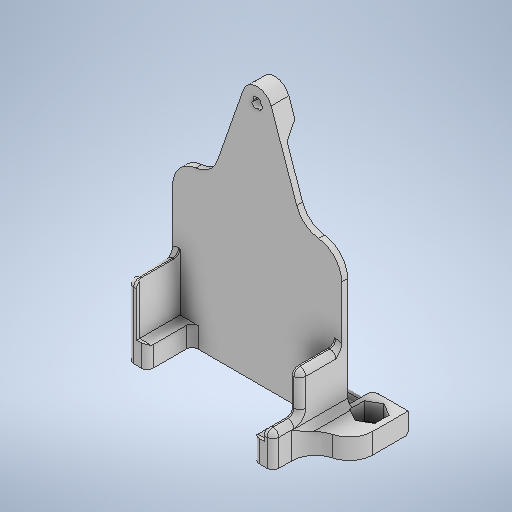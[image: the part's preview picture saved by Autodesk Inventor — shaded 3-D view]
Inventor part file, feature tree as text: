
AUTODESK INVENTOR PART (.ipt)
format: ipt  version: 2025.3 (Build 293356000, 356)  size: 1,111,552 bytes
history: native  units: in
note: dims shown in document units (in); Inventor stores cm internally (conversion verified against a paired STEP export)
features: sketch x16, extrude x14, fillet x5, chamfer x3, hole x1
ambient origin geometry x8: Origin, YZ Plane, XZ Plane, XY Plane, X Axis, Y Axis, Z Axis, Center Point
bodies: Solid1 (feature_tree)
feature tree (39):
  extrude  "Extrusion1"  Depth=0.3937in
  extrude  "Extrusion2"  Depth=0.0787in
  extrude  "Extrusion3"  Depth=0.6098in
  extrude  "Extrusion4"  Depth=0.1575in TaperAngle=0.0deg
  extrude  "Extrusion5"  Depth=0.878in TaperAngle=0.0deg
  extrude  "Extrusion6"  Depth=0.0394in TaperAngle=0.0deg
  extrude  "Extrusion8"  Depth=0.2598in
  hole  "Hole1"  [1 undecoded]
  extrude  "Extrusion15"  Depth=1.128in
  chamfer  "Chamfer1"  Distance=0.52in
  chamfer  "Chamfer2"  Distance=1.1811in Angle=360.0deg
  chamfer  "Chamfer3"  Distance=0.3937in
  extrude  "Extrusion17"  Depth=0.0787in
  extrude  "Extrusion18"  Depth=0.0787in
  fillet  "Fillet6"  Radius=0.7874in
  fillet  "Fillet7"  Radius=0.7874in
  fillet  "Fillet8"  Radius=0.0984in
  extrude  "Extrusion20"  Depth=0.0787in
  extrude  "Extrusion21"  Depth=0.0787in
  extrude  "Extrusion22"  Depth=0.0787in
  fillet  "Fillet9"  Radius=0.1181in
  fillet  "Fillet10"  Radius=0.2622in
  extrude  "Extrusion23"  Depth=0.0787in
  sketch  "Sketch1"  dims[d2=0.3937in d3=1.1516in]
  sketch  "Sketch2"  dims[d26=1.2197in d27=0.6098in]
  sketch  "Sketch3"  dims[d28=0.0in d40=0.1575in d41=0.0in]
  sketch  "Sketch4"  dims[d73=0.5593in d74=0.0in d79=0.878in d80=0.0in]
  sketch  "Sketch5"  dims[d89=0.0394in d90=0.0in d95=0.0394in d96=0.0in]
  sketch  "Sketch6"  dims[d100=0.2598in d101=0.2598in]
  sketch  "Sketch9"  dims[d102=0.0984in d103=0.0984in]
  sketch  "Sketch11"  dims[d112=2.2559in d113=1.128in]
  sketch  "Sketch18"  dims[d114=3.2323in d120=0.52in d121=0.0in]
  sketch  "Sketch Circular Pattern1"  dims[d4=0.0787in d5=0.0in d6=0.1378in d9=0.1378in d16=0.1378in]
  sketch  "Sketch20"  dims[d130=0.1476in d131=0.17in d132=0.375in d133=0.25in d134=0.5635in d135=0.4322in d136=0.0in]
  sketch  "Sketch21"  dims[d159=0.1181in]
  sketch  "Sketch23"  dims[d160=0.1181in]
  sketch  "Sketch24"  dims[d170=0.0787in]
  sketch  "Sketch25"  dims[d178=0.0443in d179=1.1811in d181=360.0deg d183=0.3937in d184=0.0in]
  sketch  "Sketch26"  dims[d188=0.1772in d189=0.1575in d190=0.0787in d191=0.7874in d192=0.7874in d194=0.0984in d195=0.0984in d196=1.1189in d197=1.1189in d198=0.1181in d199=0.2622in d200=0.2622in d201=0.1181in d202=0.0984in d203=0.2622in d204=0.2622in d205=0.0984in d206=0.9618in d207=0.1063in d208=0.1811in d209=0.0787in d210=0.0098in d211=0.0787in d212=45.0deg d213=0.0787in d214=0.0787in d215=0.1575in d216=0.1412in d217=0.0787in d218=45.0deg d219=0.0162in d220=0.0787in d221=45.0deg d222=0.3937in d223=0.0in d224=0.3937in d225=0.0in d226=0.0787in d227=0.0394in d228=0.3519in d231=0.4724in d232=0.0in d234=0.2362in d235=0.0in d237=0.0in d238=0.0in d239=0.315in d240=0.0787in d241=0.0in d242=0.0in d245=0.0in d246=0.3327in d247=0.0787in d248=0.0787in d249=0.2598in d168=0.0in d169=0.0in d171=0.0in d172=0.0in d173=0.0197in d174=0.0344in d187=0.0in d233=0.0in]
note: 1 required parameter value undecoded (feature->parameter linkage not recoverable at this tier; creation-order binding heuristic only, values carry confidence <= 0.55)
